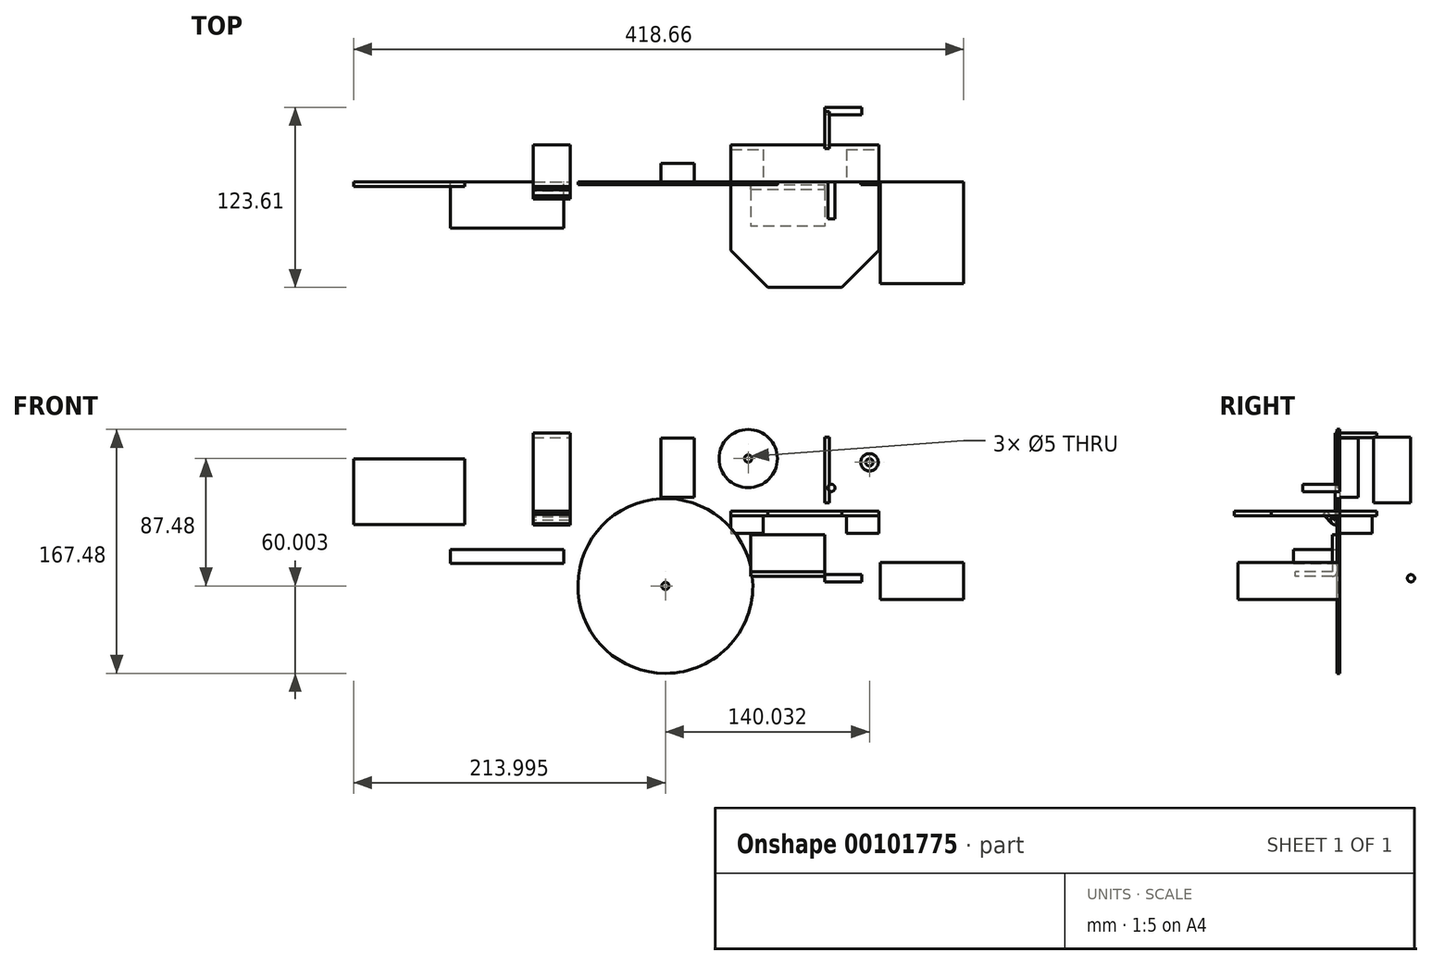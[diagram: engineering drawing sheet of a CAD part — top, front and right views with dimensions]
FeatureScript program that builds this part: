
annotation { "Feature Type Name" : "Feature", "Feature Type Description" : "" }
export const myFeature = defineFeature(function(context is Context, id is Id, definition is map)
    precondition{}
    {
        {
            var Q0;
            Q0=qCreatedBy(makeId("Front.planeOp"),FACE);
            var sketch = newSketch(context, id + "F0", { "sketchPlane" : qUnion([Q0])});
            skLineSegment(sketch, "E0.bottom", {"start": v(-64.58, 3.08) * mm, "end": v(-42.36, 3.08) * mm});
            skLineSegment(sketch, "E0.top", {"start": v(-64.58, -8.86) * mm, "end": v(-42.36, -8.86) * mm});
            skLineSegment(sketch, "E0.left", {"start": v(-64.58, 3.08) * mm, "end": v(-64.58, -8.86) * mm});
            skLineSegment(sketch, "E0.right", {"start": v(-42.36, 3.08) * mm, "end": v(-42.36, -8.86) * mm});
            skLineSegment(sketch, "E1.bottom", {"start": v(14.8, 3.08) * mm, "end": v(37.02, 3.08) * mm});
            skLineSegment(sketch, "E1.top", {"start": v(14.8, -8.86) * mm, "end": v(37.02, -8.86) * mm});
            skLineSegment(sketch, "E1.left", {"start": v(14.8, 3.08) * mm, "end": v(14.8, -8.86) * mm});
            skLineSegment(sketch, "E1.right", {"start": v(37.02, 3.08) * mm, "end": v(37.02, -8.86) * mm});
            skLineSegment(sketch, "E2", {"start": v(-75.74, 3.08) * mm, "end": v(65.58, 3.08) * mm});
            skLineSegment(sketch, "E3", {"start": v(-64.58, 3.08) * mm, "end": v(-64.58, 6.26) * mm});
            skLineSegment(sketch, "E4", {"start": v(-64.58, 6.26) * mm, "end": v(37.02, 6.26) * mm});
            skLineSegment(sketch, "E5", {"start": v(37.02, 6.26) * mm, "end": v(37.02, 3.08) * mm});
            skSolve(sketch);
        }
        {
            var Q0;
            Q0=makeQuery(id+"F0.imprint","IMPRINT",FACE,{"disambiguationData":[TD([[makeQuery(id+"F0.imprint","IMPRINT",EDGE,{"derivedFrom":sQuery(id+"F0.wireOp",EDGE,"E0.top")}),1.0]])]});
            extrude(context, id + "F1", {"entities" : qUnion([Q0]), "oppositeDirection" : true, "depth" : 22.22 * mm});
        }
        {
            var Q0;
            Q0=makeQuery(id+"F0.imprint","IMPRINT",FACE,{"disambiguationData":[TD([[makeQuery(id+"F0.imprint","IMPRINT",EDGE,{"derivedFrom":sQuery(id+"F0.wireOp",EDGE,"E1.top")}),1.0]])]});
            extrude(context, id + "F2", {"entities" : qUnion([Q0]), "oppositeDirection" : true, "depth" : 22.22 * mm});
        }
        {
            var Q0;
            Q0=qCreatedBy(makeId("Front.planeOp"),FACE);
            var sketch = newSketch(context, id + "F3", { "sketchPlane" : qUnion([Q0])});
            skLineSegment(sketch, "E6.bottom", {"start": v(-112.58, 56.48) * mm, "end": v(-89.72, 56.48) * mm});
            skLineSegment(sketch, "E6.top", {"start": v(-112.58, 15.84) * mm, "end": v(-89.72, 15.84) * mm});
            skLineSegment(sketch, "E6.left", {"start": v(-112.58, 56.48) * mm, "end": v(-112.58, 15.84) * mm});
            skLineSegment(sketch, "E6.right", {"start": v(-89.72, 56.48) * mm, "end": v(-89.72, 15.84) * mm});
            skSolve(sketch);
        }
        {
            var Q0;
            Q0=makeQuery(id+"F3.imprint","IMPRINT",FACE,{"disambiguationData":[TD([[makeQuery(id+"F3.imprint","IMPRINT",EDGE,{"derivedFrom":sQuery(id+"F3.wireOp",EDGE,"E6.bottom")}),-1.0]])]});
            extrude(context, id + "F4", {"entities" : qUnion([Q0]), "oppositeDirection" : true, "depth" : 12.7 * mm});
        }
        {
            var Q0;
            Q0=qCreatedBy(makeId("Front.planeOp"),FACE);
            var sketch = newSketch(context, id + "F5", { "sketchPlane" : qUnion([Q0])});
            skLineSegment(sketch, "E7.bottom", {"start": v(38.07, -28.9) * mm, "end": v(95.22, -28.9) * mm});
            skLineSegment(sketch, "E7.top", {"start": v(38.07, -54.3) * mm, "end": v(95.22, -54.3) * mm});
            skLineSegment(sketch, "E7.left", {"start": v(38.07, -28.9) * mm, "end": v(38.07, -54.3) * mm});
            skLineSegment(sketch, "E7.right", {"start": v(95.22, -28.9) * mm, "end": v(95.22, -54.3) * mm});
            skSolve(sketch);
        }
        {
            var Q0;
            Q0=makeQuery(id+"F5.imprint","IMPRINT",FACE,{"disambiguationData":[TD([[makeQuery(id+"F5.imprint","IMPRINT",EDGE,{"derivedFrom":sQuery(id+"F5.wireOp",EDGE,"E7.bottom")}),-1.0]])]});
            extrude(context, id + "F6", {"entities" : qUnion([Q0]), "depth" : 69.85 * mm});
        }
        {
            var Q0;
            {var subQ0=sQuery(id+"F0.wireOp",EDGE,"E3");Q0=makeQuery(id+"F0.imprint","IMPRINT",FACE,{"disambiguationData":[TD([[makeQuery(id+"F0.imprint","IMPRINT",EDGE,{"derivedFrom":subQ0}),-1.0]])]});}
            extrude(context, id + "F7", {"entities" : qUnion([Q0]), "oppositeDirection" : true, "depth" : 25.4 * mm});
        }
        {
            var Q0;
            {var subQ0=sQuery(id+"F0.wireOp",EDGE,"E3");Q0=makeQuery(id+"F0.imprint","IMPRINT",FACE,{"disambiguationData":[TD([[makeQuery(id+"F0.imprint","IMPRINT",EDGE,{"derivedFrom":subQ0}),-1.0]])]});}
            extrude(context, id + "F8", {"entities" : qUnion([Q0]), "depth" : 72.39 * mm});
        }
        {
            var Q0;
            Q0=qCreatedBy(makeId("Front.planeOp"),FACE);
            var sketch = newSketch(context, id + "F9", { "sketchPlane" : qUnion([Q0])});
            skCircle(sketch, "E8", {"center": v(-52.64, 42.42) * mm, "radius": 20 * mm});
            skSolve(sketch);
        }
        {
            var Q0;
            Q0=makeQuery(id+"F9.imprint","IMPRINT",FACE,{"disambiguationData":[TD([[makeQuery(id+"F9.imprint","IMPRINT",EDGE,{"derivedFrom":sQuery(id+"F9.wireOp",EDGE,"E8")}),1.0]])]});
            extrude(context, id + "F10", {"entities" : qUnion([Q0]), "depth" : 2 * mm});
        }
        {
            var Q0;
            Q0=qCreatedBy(makeId("Front.planeOp"),FACE);
            var sketch = newSketch(context, id + "F11", { "sketchPlane" : qUnion([Q0])});
            skCircle(sketch, "E9", {"center": v(30.59, 39.81) * mm, "radius": 6 * mm});
            skSolve(sketch);
        }
        {
            var Q0;
            Q0=makeQuery(id+"F11.imprint","IMPRINT",FACE,{"disambiguationData":[TD([[makeQuery(id+"F11.imprint","IMPRINT",EDGE,{"derivedFrom":sQuery(id+"F11.wireOp",EDGE,"E9")}),1.0]])]});
            extrude(context, id + "F12", {"entities" : qUnion([Q0]), "depth" : 2 * mm});
        }
        {
            var Q0;
            Q0=makeQuery(id+"F8.opExtrude","SWEPT_FACE",FACE,{"disambiguationData":[OSD([sQuery(id+"F0.wireOp",EDGE,"E4")])]});
            var sketch = newSketch(context, id + "F13", { "sketchPlane" : qUnion([Q0])});
            skLineSegment(sketch, "E10", {"start": v(37.02, -47) * mm, "end": v(11.62, -72.4) * mm});
            skLineSegment(sketch, "E11", {"start": v(11.62, -72.4) * mm, "end": v(-39.18, -72.4) * mm});
            skLineSegment(sketch, "E12", {"start": v(-39.18, -72.4) * mm, "end": v(-64.58, -47) * mm});
            skSolve(sketch);
        }
        {
            var Q0;
            {var subQ0=sQuery(id+"F13.wireOp",EDGE,"E12");Q0=makeQuery(id+"F13.imprint","IMPRINT",FACE,{"disambiguationData":[TD([[makeQuery(id+"F13.imprint","IMPRINT",EDGE,{"derivedFrom":subQ0}),1.0]])]});}
            var Q1;
            {var subQ0=sQuery(id+"F13.wireOp",EDGE,"E10");Q1=makeQuery(id+"F13.imprint","IMPRINT",FACE,{"disambiguationData":[TD([[makeQuery(id+"F13.imprint","IMPRINT",EDGE,{"derivedFrom":subQ0}),1.0]])]});}
            extrude(context, id + "F14", {"entities" : qUnion([Q0, Q1]), "operationType" : NewBodyOperationType.REMOVE, "oppositeDirection" : true, "depth" : 25.4 * mm});
        }
        {
            var Q0;
            Q0=makeQuery(id+"F10.opExtrude","CAP_FACE",FACE,{"disambiguationData":[OSD([sQuery(id+"F9.wireOp",EDGE,"E8")])],"isStart":false});
            var sketch = newSketch(context, id + "F15", { "sketchPlane" : qUnion([Q0])});
            skLineSegment(sketch, "E13.bottom", {"start": v(-51.01, -9.86) * mm, "end": v(-0.21, -9.86) * mm});
            skLineSegment(sketch, "E13.top", {"start": v(-51.01, -35.26) * mm, "end": v(-0.21, -35.26) * mm});
            skLineSegment(sketch, "E13.left", {"start": v(-51.01, -9.86) * mm, "end": v(-51.01, -35.26) * mm});
            skLineSegment(sketch, "E13.right", {"start": v(-0.21, -9.86) * mm, "end": v(-0.21, -35.26) * mm});
            skSolve(sketch);
        }
        {
            var Q0;
            Q0=makeQuery(id+"F15.imprint","IMPRINT",FACE,{"disambiguationData":[TD([[makeQuery(id+"F15.imprint","IMPRINT",EDGE,{"derivedFrom":sQuery(id+"F15.wireOp",EDGE,"E13.bottom")}),-1.0]])]});
            extrude(context, id + "F16", {"entities" : qUnion([Q0]), "depth" : 3.17 * mm});
        }
        {
            var Q0;
            Q0=makeQuery(id+"F16.opExtrude","CAP_FACE",FACE,{"disambiguationData":[OSD([sQuery(id+"F15.wireOp",EDGE,"E13.bottom"),sQuery(id+"F15.wireOp",EDGE,"E13.left"),sQuery(id+"F15.wireOp",EDGE,"E13.right"),sQuery(id+"F15.wireOp",EDGE,"E13.top")])],"isStart":false});
            var sketch = newSketch(context, id + "F17", { "sketchPlane" : qUnion([Q0])});
            skLineSegment(sketch, "E14", {"start": v(-51.01, -35.26) * mm, "end": v(-51.01, -32.09) * mm});
            skLineSegment(sketch, "E15", {"start": v(-51.01, -32.09) * mm, "end": v(-0.21, -32.09) * mm});
            skLineSegment(sketch, "E16", {"start": v(-0.21, -32.09) * mm, "end": v(-0.21, -35.26) * mm});
            skSolve(sketch);
        }
        {
            var Q0;
            Q0=makeQuery(id+"F17.imprint","IMPRINT",FACE,{"disambiguationData":[TD([[makeQuery(id+"F17.imprint","IMPRINT",EDGE,{"derivedFrom":sQuery(id+"F17.wireOp",EDGE,"E14")}),1.0]])]});
            var Q1;
            Q1=makeQuery(id+"F16.opExtrude","CAP_EDGE",EDGE,{"disambiguationData":[OSD([sQuery(id+"F15.wireOp",EDGE,"E13.top")])],"isStart":false});
            revolve(context, id + "F18", {"operationType" : NewBodyOperationType.ADD, "entities" : qUnion([Q0]), "axis" : qUnion([Q1]), "revolveType" : RevolveType.FULL});
        }
        {
            var Q0;
            Q0=makeQuery(id+"F18.boolean.opBoolean","MERGE",FACE,{"derivedFrom":[makeQuery(id+"F16.opExtrude","SWEPT_FACE",FACE,{"disambiguationData":[OSD([sQuery(id+"F15.wireOp",EDGE,"E13.left")])]}),makeQuery(id+"F18.opRevolve","SWEPT_FACE",FACE,{"disambiguationData":[OSD([sQuery(id+"F17.wireOp",EDGE,"E14")])]})]});
            var sketch = newSketch(context, id + "F19", { "sketchPlane" : qUnion([Q0])});
            skLineSegment(sketch, "E17", {"start": v(5.18, -32.09) * mm, "end": v(5.18, -35.26) * mm});
            skLineSegment(sketch, "E18", {"start": v(5.18, -35.26) * mm, "end": v(8.35, -35.26) * mm});
            skSolve(sketch);
        }
        {
            var Q0;
            {var subQ0=sQuery(id+"F19.wireOp",EDGE,"E17");Q0=makeQuery(id+"F19.imprint","IMPRINT",FACE,{"disambiguationData":[TD([[makeQuery(id+"F19.imprint","IMPRINT",EDGE,{"derivedFrom":subQ0}),1.0]])]});}
            extrude(context, id + "F20", {"entities" : qUnion([Q0]), "operationType" : NewBodyOperationType.REMOVE, "oppositeDirection" : true, "depth" : 50.8 * mm});
        }
        {
            var Q0;
            Q0=makeQuery(id+"F18.boolean.opBoolean","MERGE",FACE,{"derivedFrom":[makeQuery(id+"F16.opExtrude","SWEPT_FACE",FACE,{"disambiguationData":[OSD([sQuery(id+"F15.wireOp",EDGE,"E13.left")])]}),makeQuery(id+"F18.opRevolve","SWEPT_FACE",FACE,{"disambiguationData":[OSD([sQuery(id+"F17.wireOp",EDGE,"E14")])]})]});
            var sketch = newSketch(context, id + "F21", { "sketchPlane" : qUnion([Q0])});
            skLineSegment(sketch, "E19", {"start": v(5.18, -35.26) * mm, "end": v(5.18, -38.44) * mm});
            skLineSegment(sketch, "E20", {"start": v(5.18, -38.44) * mm, "end": v(30.57, -38.44) * mm});
            skLineSegment(sketch, "E21", {"start": v(30.58, -35.26) * mm, "end": v(5.17, -35.26) * mm});
            skLineSegment(sketch, "E22", {"start": v(30.57, -38.44) * mm, "end": v(30.57, -35.26) * mm});
            skSolve(sketch);
        }
        {
            var Q0;
            {var subQ0=sQuery(id+"F21.wireOp",EDGE,"E20");Q0=makeQuery(id+"F21.imprint","IMPRINT",FACE,{"disambiguationData":[TD([[makeQuery(id+"F21.imprint","IMPRINT",EDGE,{"derivedFrom":subQ0}),1.0]])]});}
            extrude(context, id + "F22", {"entities" : qUnion([Q0]), "operationType" : NewBodyOperationType.ADD, "oppositeDirection" : true, "depth" : 50.8 * mm});
        }
        {
            var Q0;
            Q0=qCreatedBy(makeId("Front.planeOp"),FACE);
            var sketch = newSketch(context, id + "F23", { "sketchPlane" : qUnion([Q0])});
            skCircle(sketch, "E23", {"center": v(-109.44, -45.06) * mm, "radius": 60 * mm});
            skSolve(sketch);
        }
        {
            var Q0;
            Q0=makeQuery(id+"F23.imprint","IMPRINT",FACE,{"disambiguationData":[TD([[makeQuery(id+"F23.imprint","IMPRINT",EDGE,{"derivedFrom":sQuery(id+"F23.wireOp",EDGE,"E23")}),1.0]])]});
            extrude(context, id + "F24", {"entities" : qUnion([Q0]), "depth" : 2 * mm});
        }
        {
            var Q0;
            Q0=makeQuery(id+"F24.opExtrude","CAP_FACE",FACE,{"disambiguationData":[OSD([sQuery(id+"F23.wireOp",EDGE,"E23")])],"isStart":false});
            var sketch = newSketch(context, id + "F25", { "sketchPlane" : qUnion([Q0])});
            skCircle(sketch, "E24", {"center": v(-109.44, -45.06) * mm, "radius": 2.5 * mm});
            skSolve(sketch);
        }
        {
            var Q0;
            Q0=makeQuery(id+"F25.imprint","IMPRINT",FACE,{"disambiguationData":[TD([[makeQuery(id+"F25.imprint","IMPRINT",EDGE,{"derivedFrom":sQuery(id+"F25.wireOp",EDGE,"E24")}),1.0]])]});
            extrude(context, id + "F26", {"entities" : qUnion([Q0]), "operationType" : NewBodyOperationType.REMOVE, "oppositeDirection" : true, "depth" : 25.4 * mm});
        }
        {
            var Q0;
            Q0=makeQuery(id+"F10.opExtrude","CAP_FACE",FACE,{"disambiguationData":[OSD([sQuery(id+"F9.wireOp",EDGE,"E8")])],"isStart":false});
            var sketch = newSketch(context, id + "F27", { "sketchPlane" : qUnion([Q0])});
            skCircle(sketch, "E25", {"center": v(-52.64, 42.42) * mm, "radius": 2.5 * mm});
            skSolve(sketch);
        }
        {
            var Q0;
            Q0=makeQuery(id+"F27.imprint","IMPRINT",FACE,{"disambiguationData":[TD([[makeQuery(id+"F27.imprint","IMPRINT",EDGE,{"derivedFrom":sQuery(id+"F27.wireOp",EDGE,"E25")}),1.0]])]});
            extrude(context, id + "F28", {"entities" : qUnion([Q0]), "operationType" : NewBodyOperationType.REMOVE, "oppositeDirection" : true, "depth" : 25.4 * mm});
        }
        {
            var Q0;
            Q0=makeQuery(id+"F12.opExtrude","CAP_FACE",FACE,{"disambiguationData":[OSD([sQuery(id+"F11.wireOp",EDGE,"E9")])],"isStart":false});
            var sketch = newSketch(context, id + "F29", { "sketchPlane" : qUnion([Q0])});
            skCircle(sketch, "E26", {"center": v(30.59, 39.81) * mm, "radius": 2.5 * mm});
            skSolve(sketch);
        }
        {
            var Q0;
            Q0=makeQuery(id+"F29.imprint","IMPRINT",FACE,{"disambiguationData":[TD([[makeQuery(id+"F29.imprint","IMPRINT",EDGE,{"derivedFrom":sQuery(id+"F29.wireOp",EDGE,"E26")}),1.0]])]});
            extrude(context, id + "F30", {"entities" : qUnion([Q0]), "operationType" : NewBodyOperationType.REMOVE, "oppositeDirection" : true, "depth" : 25.4 * mm});
        }
        {
            var Q0;
            Q0=qCreatedBy(makeId("Front.planeOp"),FACE);
            var sketch = newSketch(context, id + "F31", { "sketchPlane" : qUnion([Q0])});
            skCircle(sketch, "E27", {"center": v(4.46, 22.27) * mm, "radius": 2.5 * mm});
            skSolve(sketch);
        }
        {
            var Q0;
            Q0=makeQuery(id+"F31.imprint","IMPRINT",FACE,{"disambiguationData":[TD([[makeQuery(id+"F31.imprint","IMPRINT",EDGE,{"derivedFrom":sQuery(id+"F31.wireOp",EDGE,"E27")}),1.0]])]});
            extrude(context, id + "F32", {"entities" : qUnion([Q0]), "depth" : 25.4 * mm});
        }
        {
            var Q0;
            Q0=qCreatedBy(makeId("Front.planeOp"),FACE);
            var sketch = newSketch(context, id + "F33", { "sketchPlane" : qUnion([Q0])});
            skLineSegment(sketch, "E28.bottom", {"start": v(-256.9, -19.94) * mm, "end": v(-179.12, -19.94) * mm});
            skLineSegment(sketch, "E28.top", {"start": v(-256.9, -29.46) * mm, "end": v(-179.12, -29.46) * mm});
            skLineSegment(sketch, "E28.left", {"start": v(-256.9, -19.94) * mm, "end": v(-256.9, -29.46) * mm});
            skLineSegment(sketch, "E28.right", {"start": v(-179.12, -19.94) * mm, "end": v(-179.12, -29.46) * mm});
            skSolve(sketch);
        }
        {
            var Q0;
            Q0=makeQuery(id+"F33.imprint","IMPRINT",FACE,{"disambiguationData":[TD([[makeQuery(id+"F33.imprint","IMPRINT",EDGE,{"derivedFrom":sQuery(id+"F33.wireOp",EDGE,"E28.bottom")}),-1.0]])]});
            extrude(context, id + "F34", {"entities" : qUnion([Q0]), "depth" : 31.75 * mm});
        }
        {
            var Q0;
            Q0=qCreatedBy(makeId("Front.planeOp"),FACE);
            var sketch = newSketch(context, id + "F35", { "sketchPlane" : qUnion([Q0])});
            skLineSegment(sketch, "E29.bottom", {"start": v(-200.26, 60.07) * mm, "end": v(-174.86, 60.07) * mm});
            skLineSegment(sketch, "E29.top", {"start": v(-200.26, 0.07) * mm, "end": v(-174.86, 0.07) * mm});
            skLineSegment(sketch, "E29.left", {"start": v(-200.26, 60.07) * mm, "end": v(-200.26, 0.07) * mm});
            skLineSegment(sketch, "E29.right", {"start": v(-174.86, 60.07) * mm, "end": v(-174.86, 0.07) * mm});
            skSolve(sketch);
        }
        {
            var Q0;
            Q0=makeQuery(id+"F35.imprint","IMPRINT",FACE,{"disambiguationData":[TD([[makeQuery(id+"F35.imprint","IMPRINT",EDGE,{"derivedFrom":sQuery(id+"F35.wireOp",EDGE,"E29.bottom")}),-1.0]])]});
            extrude(context, id + "F36", {"entities" : qUnion([Q0]), "depth" : 3.17 * mm});
        }
        {
            var Q0;
            Q0=makeQuery(id+"F36.opExtrude","CAP_FACE",FACE,{"disambiguationData":[OSD([sQuery(id+"F35.wireOp",EDGE,"E29.bottom"),sQuery(id+"F35.wireOp",EDGE,"E29.top"),sQuery(id+"F35.wireOp",EDGE,"E29.left"),sQuery(id+"F35.wireOp",EDGE,"E29.right")])],"isStart":false});
            var sketch = newSketch(context, id + "F37", { "sketchPlane" : qUnion([Q0])});
            skLineSegment(sketch, "E30", {"start": v(-200.26, 0.07) * mm, "end": v(-174.86, 0.07) * mm});
            skLineSegment(sketch, "E31", {"start": v(-174.86, 0.07) * mm, "end": v(-174.86, 3.24) * mm});
            skLineSegment(sketch, "E32", {"start": v(-174.86, 3.24) * mm, "end": v(-200.26, 3.24) * mm});
            skLineSegment(sketch, "E33", {"start": v(-200.26, 3.24) * mm, "end": v(-200.26, 0.07) * mm});
            skSolve(sketch);
        }
        {
            var Q0;
            Q0=makeQuery(id+"F37.imprint","IMPRINT",FACE,{"disambiguationData":[TD([[makeQuery(id+"F37.imprint","IMPRINT",EDGE,{"derivedFrom":sQuery(id+"F37.wireOp",EDGE,"E30")}),1.0]])]});
            var Q1;
            Q1=sQuery(id+"F37.wireOp",EDGE,"E30");
            revolve(context, id + "F38", {"operationType" : NewBodyOperationType.ADD, "entities" : qUnion([Q0]), "axis" : qUnion([Q1]), "revolveType" : RevolveType.FULL});
        }
        {
            var Q0;
            Q0=makeQuery(id+"F38.boolean.opBoolean","MERGE",FACE,{"derivedFrom":[makeQuery(id+"F36.opExtrude","SWEPT_FACE",FACE,{"disambiguationData":[OSD([sQuery(id+"F35.wireOp",EDGE,"E29.left")])]}),makeQuery(id+"F38.opRevolve","SWEPT_FACE",FACE,{"disambiguationData":[OSD([sQuery(id+"F37.wireOp",EDGE,"E33")])]})]});
            var sketch = newSketch(context, id + "F39", { "sketchPlane" : qUnion([Q0])});
            skLineSegment(sketch, "E34", {"start": v(3.18, 3.24) * mm, "end": v(3.18, 0.07) * mm});
            skLineSegment(sketch, "E35", {"start": v(3.18, 0.07) * mm, "end": v(9.46, 6.35) * mm});
            skLineSegment(sketch, "E36", {"start": v(9.46, 6.35) * mm, "end": v(11.7, 4.1) * mm});
            skLineSegment(sketch, "E37", {"start": v(11.7, 4.1) * mm, "end": v(4.9, -2.7) * mm});
            skSolve(sketch);
        }
        {
            var Q0;
            {var subQ0=sQuery(id+"F39.wireOp",EDGE,"E36");Q0=makeQuery(id+"F39.imprint","IMPRINT",FACE,{"disambiguationData":[TD([[makeQuery(id+"F39.imprint","IMPRINT",EDGE,{"derivedFrom":subQ0}),-1.0]])]});}
            extrude(context, id + "F40", {"entities" : qUnion([Q0]), "oppositeDirection" : true, "depth" : 25.4 * mm});
        }
        {
            var Q0;
            {var subQ0=sQuery(id+"F39.wireOp",EDGE,"E34");Q0=makeQuery(id+"F39.imprint","IMPRINT",FACE,{"disambiguationData":[TD([[makeQuery(id+"F39.imprint","IMPRINT",EDGE,{"derivedFrom":subQ0}),1.0]])]});}
            extrude(context, id + "F41", {"entities" : qUnion([Q0]), "operationType" : NewBodyOperationType.REMOVE, "oppositeDirection" : true, "depth" : 25.4 * mm});
        }
        {
            var Q0;
            {var subQ0=sQuery(id+"F37.wireOp",EDGE,"E32");Q0=makeQuery(id+"F37.imprint","IMPRINT",FACE,{"disambiguationData":[TD([[makeQuery(id+"F37.imprint","IMPRINT",EDGE,{"derivedFrom":subQ0}),-1.0]])]});}
            var sketch = newSketch(context, id + "F42", { "sketchPlane" : qUnion([Q0])});
            skLineSegment(sketch, "E38", {"start": v(-200.26, 60.07) * mm, "end": v(-200.26, 56.9) * mm});
            skLineSegment(sketch, "E39", {"start": v(-200.26, 56.9) * mm, "end": v(-174.86, 56.9) * mm});
            skLineSegment(sketch, "E40", {"start": v(-174.86, 56.9) * mm, "end": v(-174.86, 60.07) * mm});
            skLineSegment(sketch, "E41", {"start": v(-174.86, 60.07) * mm, "end": v(-200.26, 60.07) * mm});
            skSolve(sketch);
        }
        {
            var Q0;
            Q0=makeQuery(id+"F42.imprint","IMPRINT",FACE,{"disambiguationData":[TD([[makeQuery(id+"F42.imprint","IMPRINT",EDGE,{"derivedFrom":sQuery(id+"F42.wireOp",EDGE,"E38")}),1.0]])]});
            extrude(context, id + "F43", {"entities" : qUnion([Q0]), "operationType" : NewBodyOperationType.ADD, "oppositeDirection" : true, "depth" : 28.57 * mm});
        }
        {
            var Q0;
            Q0=qCreatedBy(makeId("Front.planeOp"),FACE);
            var sketch = newSketch(context, id + "F44", { "sketchPlane" : qUnion([Q0])});
            skLineSegment(sketch, "E42.bottom", {"start": v(-323.44, 42.14) * mm, "end": v(-247.24, 42.14) * mm});
            skLineSegment(sketch, "E42.top", {"start": v(-323.44, -2.86) * mm, "end": v(-247.24, -2.86) * mm});
            skLineSegment(sketch, "E42.left", {"start": v(-323.44, 42.14) * mm, "end": v(-323.44, -2.86) * mm});
            skLineSegment(sketch, "E42.right", {"start": v(-247.24, 42.14) * mm, "end": v(-247.24, -2.86) * mm});
            skSolve(sketch);
        }
        {
            var Q0;
            Q0=makeQuery(id+"F44.imprint","IMPRINT",FACE,{"disambiguationData":[TD([[makeQuery(id+"F44.imprint","IMPRINT",EDGE,{"derivedFrom":sQuery(id+"F44.wireOp",EDGE,"E42.bottom")}),-1.0]])]});
            extrude(context, id + "F45", {"entities" : qUnion([Q0]), "operationType" : NewBodyOperationType.ADD, "depth" : 3.17 * mm});
        }
        {
            var Q0;
            Q0=qCreatedBy(makeId("Right.planeOp"),FACE);
            var sketch = newSketch(context, id + "F46", { "sketchPlane" : qUnion([Q0])});
            skLineSegment(sketch, "E43.bottom", {"start": v(48.3, 56.95) * mm, "end": v(22.9, 56.95) * mm});
            skLineSegment(sketch, "E43.top", {"start": v(48.3, 11.95) * mm, "end": v(22.9, 11.95) * mm});
            skLineSegment(sketch, "E43.left", {"start": v(48.3, 56.95) * mm, "end": v(48.3, 11.95) * mm});
            skLineSegment(sketch, "E43.right", {"start": v(22.9, 56.95) * mm, "end": v(22.9, 11.95) * mm});
            skSolve(sketch);
        }
        {
            var Q0;
            Q0=makeQuery(id+"F46.imprint","IMPRINT",FACE,{"disambiguationData":[TD([[makeQuery(id+"F46.imprint","IMPRINT",EDGE,{"derivedFrom":sQuery(id+"F46.wireOp",EDGE,"E43.bottom")}),1.0]])]});
            extrude(context, id + "F47", {"entities" : qUnion([Q0]), "depth" : 3.17 * mm});
        }
        {
            var Q0;
            Q0=qCreatedBy(makeId("Right.planeOp"),FACE);
            var sketch = newSketch(context, id + "F48", { "sketchPlane" : qUnion([Q0])});
            skCircle(sketch, "E44", {"center": v(48.72, -39.76) * mm, "radius": 2.5 * mm});
            skSolve(sketch);
        }
        {
            var Q0;
            Q0=makeQuery(id+"F48.imprint","IMPRINT",FACE,{"disambiguationData":[TD([[makeQuery(id+"F48.imprint","IMPRINT",EDGE,{"derivedFrom":sQuery(id+"F48.wireOp",EDGE,"E44")}),1.0]])]});
            extrude(context, id + "F49", {"entities" : qUnion([Q0]), "depth" : 25.4 * mm});
        }
    });
